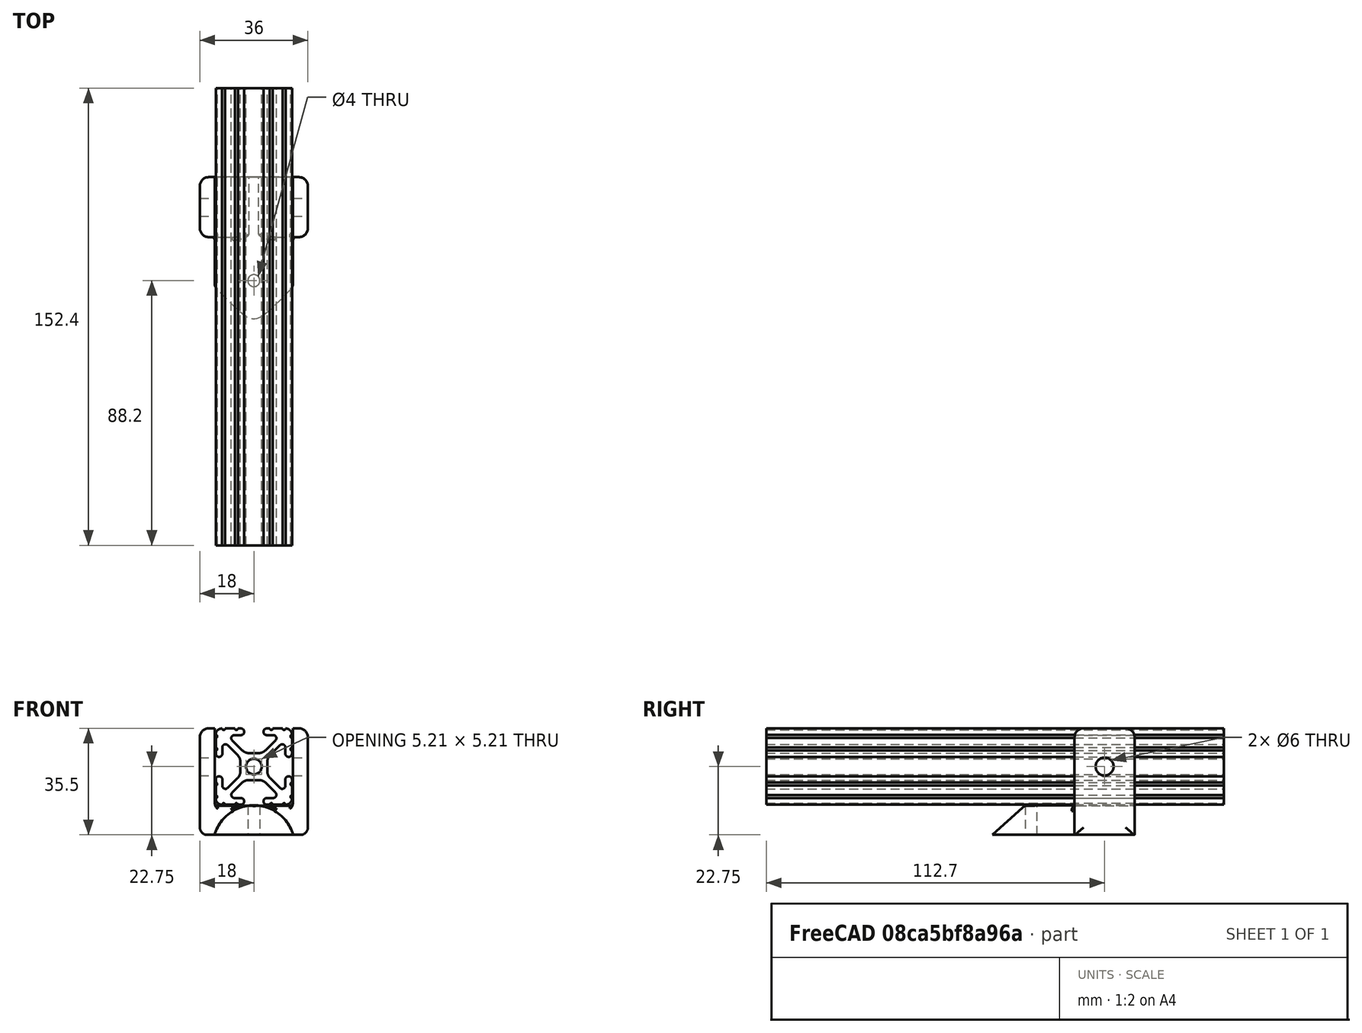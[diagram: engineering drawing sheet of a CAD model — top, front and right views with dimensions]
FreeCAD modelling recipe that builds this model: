
FCSTD DOCUMENT  (FreeCAD 0.20R29410 (Git))
Label: airModuleHolder11_22_2022
License: All rights reserved
LicenseURL: http://en.wikipedia.org/wiki/All_rights_reserved
objects: Part::Cut×6, Part::Cylinder×5, Part::Box×5, Part::Fillet×5, Part::MultiFuse×3, Part::Cone×1, Part::Feature×1
note: 26 computed .brp shape members not serialized (recipe doc carries the construction recipe); baked Part::Feature solids carry a one-line shape summary decoded from their .brp

FEATURE [Part::Cylinder] Cylinder
  Angle = 360
  AttacherType = Attacher::AttachEngine3D
  FirstAngle = 0
  Height = 36.5
  Placement = pos=(13.5,47.5,43) rot=(0,0.707107,-0.707107;3.14159rad)
  Radius = 13.6
  SecondAngle = 0
FEATURE [Part::Box] Box015  label="TSlotMount001"
  AttacherType = Attacher::AttachEngine3D
  Height = 35.5
  Length = 36
  Placement = pos=(-4.5,27.5,46.75) rot=(0,0,1;0rad)
  Width = 20
FEATURE [Part::Cylinder] Cylinder009  label="m5Cut"
  Angle = 360
  AttacherType = Attacher::AttachEngine3D
  FirstAngle = 0
  Height = 100
  Placement = pos=(-57.4,37.5,69.5) rot=(0,1,0;1.5708rad)
  Radius = 3
  SecondAngle = 0
FEATURE [Part::Box] Box016  label="Shell_Holder002"
  AttacherType = Attacher::AttachEngine3D
  Height = 20
  Length = 29
  Placement = pos=(-1,-20.5,26.75) rot=(0,0,1;0rad)
  Width = 75
FEATURE [Part::Box] Box018  label="TSlotFrameCut001"
  AttacherType = Attacher::AttachEngine3D
  Height = 28.5
  Length = 26
  Placement = pos=(0.5,0,56.5) rot=(0,0,1;0rad)
  Width = 254
FEATURE [Part::Cut] Cut009  label="TSlotMount002"
  Base = -> Box015
  Tool = -> Box018
FEATURE [Part::Cylinder] Cylinder015
  Angle = 360
  AttacherType = Attacher::AttachEngine3D
  FirstAngle = 0
  Height = 12
  Placement = pos=(13.5,13,45) rot=(0,0,1;1.5708rad)
  Radius = 2
  SecondAngle = 0
FEATURE [Part::Cone] Cone
  Angle = 180
  AttacherType = Attacher::AttachEngine3D
  Height = 15
  Placement = pos=(13.5,11,43) rot=(1,0,0;1.5708rad)
  Radius1 = 13.6
  Radius2 = 0
FEATURE [Part::MultiFuse] Fusion  label="beak"
  Shapes = -> [Cylinder,Cone]
FEATURE [Part::Cut] Cut
  Base = -> Fusion
  Tool = -> Box016
FEATURE [Part::Cut] Cut010
  Base = -> Cut009
  Tool = -> Cylinder009
FEATURE [Part::MultiFuse] Fusion002
  Shapes = -> [Cut,Cut010]
FEATURE [Part::Feature] Part__Feature  label="47065T801_T-Slotted Framing"
  Placement = pos=(13.5,1,69.5) rot=(1,0,0;1.5708rad)
  shape: bbox 25.4 x 152.4 x 25.4 mm, 108 faces (baked)
FEATURE [Part::Cylinder] Cylinder016
  Angle = 90
  AttacherType = Attacher::AttachEngine3D
  FirstAngle = 0
  Height = 50
  Placement = pos=(-2,50,49.25) rot=(0,0.707107,-0.707107;3.14159rad)
  Radius = 2.5
  SecondAngle = 0
FEATURE [Part::Box] Box019  label="Cube"
  AttacherType = Attacher::AttachEngine3D
  Height = 2.5
  Length = 2.5
  Placement = pos=(-4.5,0,46.75) rot=(0,0,1;0rad)
  Width = 50
FEATURE [Part::Cut] Cut012
  Base = -> Box019
  Tool = -> Cylinder016
FEATURE [Part::Box] Box020  label="Cube001"
  AttacherType = Attacher::AttachEngine3D
  Height = 2.5
  Length = 2.5
  Placement = pos=(-4.5,0,46.75) rot=(0,0,1;0rad)
  Width = 50
FEATURE [Part::Cylinder] Cylinder017
  Angle = 90
  AttacherType = Attacher::AttachEngine3D
  FirstAngle = 0
  Height = 50
  Placement = pos=(-2,50,49.25) rot=(0,0.707107,-0.707107;3.14159rad)
  Radius = 2.5
  SecondAngle = 0
FEATURE [Part::Cut] Cut013
  Base = -> Box020
  Placement = pos=(78.25,0,51.25) rot=(0,-1,0;1.5708rad)
  Tool = -> Cylinder017
FEATURE [Part::Fillet] Fillet
  Base = -> Fusion002
  Edges = 6 edges r=1: [Edge26,Edge28,Edge36,Edge38,Edge44,Edge46]
FEATURE [Part::Fillet] Fillet001
  Base = -> Fillet
  Edges = 2 edges r=3: [Edge4,Edge26]
FEATURE [Part::Fillet] Fillet002
  Base = -> Fillet001
  Edges = 2 edges r=3: [Edge48,Edge71]
FEATURE [Part::Fillet] Fillet003
  Base = -> Fillet002
  Edges = 1 edges r=3: [Edge57]
FEATURE [Part::Fillet] Fillet004
  Base = -> Fillet003
  Edges = 2 edges r=3: [Edge60,Edge73]
FEATURE [Part::MultiFuse] Fusion003  label="cuts"
  Shapes = -> [Cut013,Cut012,Cylinder015]
FEATURE [Part::Cut] Cut014
  Base = -> Fillet004
  Tool = -> Fusion003
